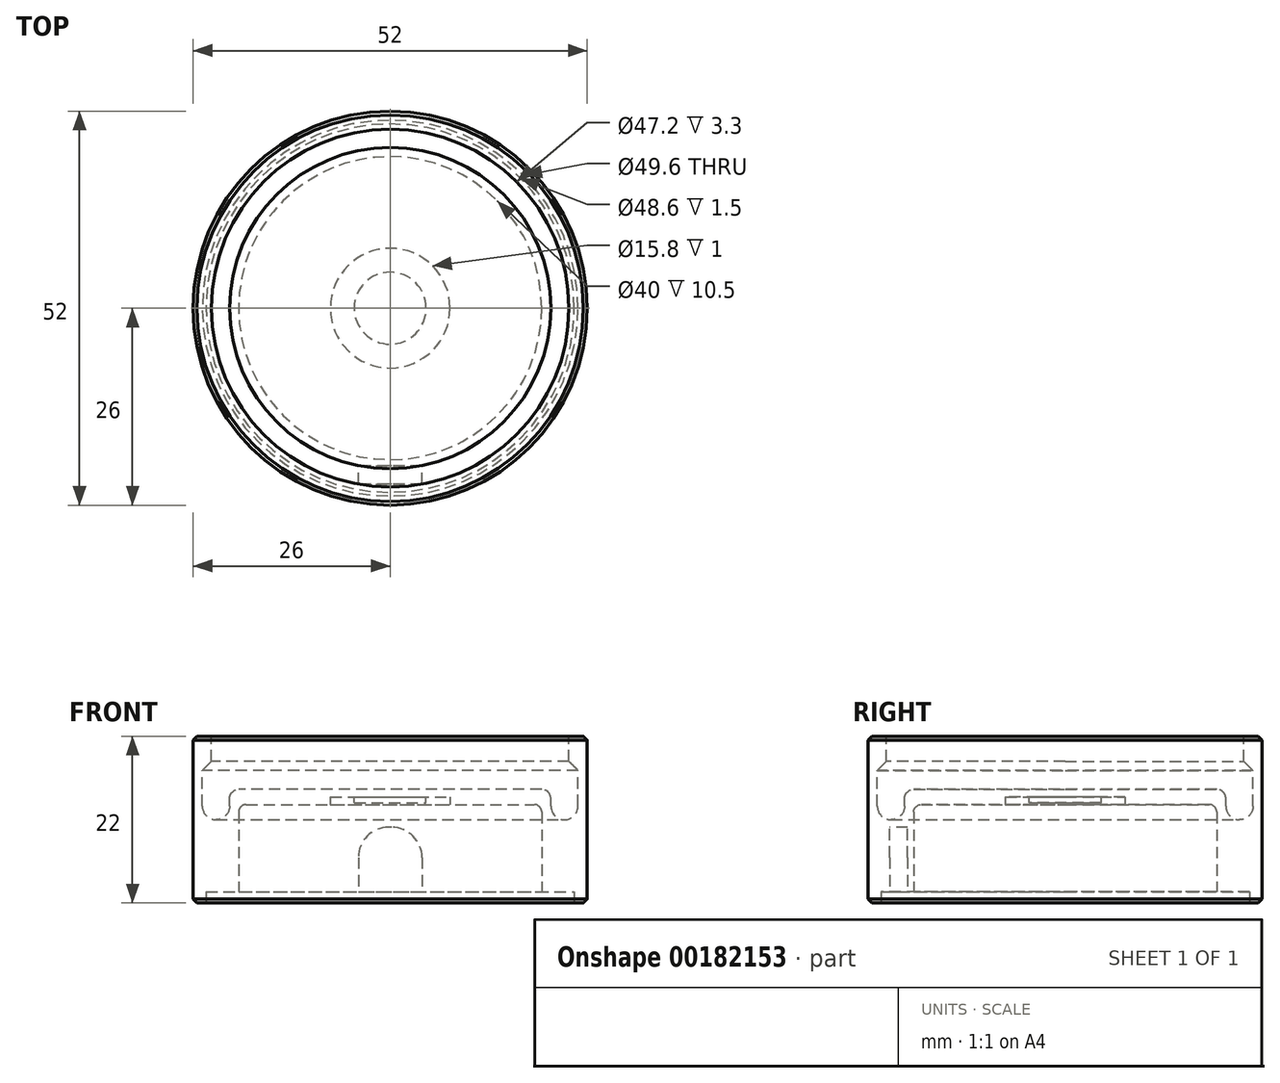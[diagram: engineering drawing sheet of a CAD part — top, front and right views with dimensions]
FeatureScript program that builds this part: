
annotation { "Feature Type Name" : "Feature", "Feature Type Description" : "" }
export const myFeature = defineFeature(function(context is Context, id is Id, definition is map)
    precondition{}
    {
        {
            var Q0;
            Q0=qCreatedBy(makeId("Top.planeOp"),FACE);
            var sketch = newSketch(context, id + "F0", { "sketchPlane" : qUnion([Q0])});
            skCircle(sketch, "E0", {"center": v(0, 0) * mm, "radius": 26 * mm});
            skSolve(sketch);
        }
        {
            var Q0;
            Q0 = qSketchRegion(id + "F0", true);
            extrude(context, id + "F1", {"entities" : qUnion([Q0]), "depth" : 22 * mm});
        }
        {
            var Q0;
            Q0=makeQuery(id+"F1.opExtrude","CAP_FACE",FACE,{"disambiguationData":[OSD([sQuery(id+"F0.wireOp",EDGE,"E0")])],"isStart":true});
            var sketch = newSketch(context, id + "F2", { "sketchPlane" : qUnion([Q0])});
            skLineSegment(sketch, "E1.bottom", {"start": v(4.2, 20.8) * mm, "end": v(-4.2, 20.8) * mm});
            skLineSegment(sketch, "E1.top", {"start": v(4.2, 23.2) * mm, "end": v(-4.2, 23.2) * mm});
            skLineSegment(sketch, "E1.left", {"start": v(4.2, 20.8) * mm, "end": v(4.2, 23.2) * mm});
            skLineSegment(sketch, "E1.right", {"start": v(-4.2, 20.8) * mm, "end": v(-4.2, 23.2) * mm});
            skPoint(sketch, "E1.middle", {"position": v(0, 22) * mm});
            skSolve(sketch);
        }
        {
            var Q0;
            Q0 = qSketchRegion(id + "F2", true);
            extrude(context, id + "F3", {"entities" : qUnion([Q0]), "operationType" : NewBodyOperationType.REMOVE, "oppositeDirection" : true, "depth" : 10 * mm});
        }
        {
            var Q0;
            Q0=makeQuery(id+"F3.boolean.opBoolean","COPY",EDGE,{"derivedFrom":makeQuery(id+"F3.opExtrude","CAP_EDGE",EDGE,{"disambiguationData":[OSD([sQuery(id+"F2.wireOp",EDGE,"E1.left")])],"isStart":false})});
            var Q1;
            Q1=makeQuery(id+"F3.boolean.opBoolean","COPY",EDGE,{"derivedFrom":makeQuery(id+"F3.opExtrude","CAP_EDGE",EDGE,{"disambiguationData":[OSD([sQuery(id+"F2.wireOp",EDGE,"E1.right")])],"isStart":false})});
            fillet(context, id + "F4", {"entities" : qUnion([Q0, Q1]), "radius" : 4 * mm, "tangentPropagation" : true, "allowEdgeOverflow" : false});
        }
        {
            var Q0;
            Q0=makeQuery(id+"F1.opExtrude","CAP_FACE",FACE,{"disambiguationData":[OSD([sQuery(id+"F0.wireOp",EDGE,"E0")])],"isStart":true});
            var sketch = newSketch(context, id + "F5", { "sketchPlane" : qUnion([Q0])});
            skCircle(sketch, "E2", {"center": v(0, 0) * mm, "radius": 20 * mm});
            skSolve(sketch);
        }
        {
            var Q0;
            Q0 = qSketchRegion(id + "F5", true);
            extrude(context, id + "F6", {"entities" : qUnion([Q0]), "operationType" : NewBodyOperationType.REMOVE, "oppositeDirection" : true, "depth" : 13 * mm});
        }
        {
            var Q0;
            Q0=makeQuery(id+"F6.boolean.opBoolean","COPY",FACE,{"derivedFrom":makeQuery(id+"F6.opExtrude","CAP_FACE",FACE,{"disambiguationData":[OSD([sQuery(id+"F5.wireOp",EDGE,"E2")])],"isStart":false})});
            var sketch = newSketch(context, id + "F7", { "sketchPlane" : qUnion([Q0])});
            skCircle(sketch, "E3", {"center": v(0, 0) * mm, "radius": 7.9 * mm});
            skSolve(sketch);
        }
        {
            var Q0;
            Q0=makeQuery(id+"F7.imprint","IMPRINT",FACE,{"disambiguationData":[TD([[makeQuery(id+"F7.imprint","IMPRINT",EDGE,{"derivedFrom":sQuery(id+"F7.wireOp",EDGE,"E3")}),1.0]])]});
            extrude(context, id + "F8", {"entities" : qUnion([Q0]), "operationType" : NewBodyOperationType.REMOVE, "oppositeDirection" : true, "depth" : 1 * mm});
        }
        {
            var Q0;
            Q0=makeQuery(id+"F8.boolean.opBoolean","COPY",FACE,{"derivedFrom":makeQuery(id+"F8.opExtrude","CAP_FACE",FACE,{"disambiguationData":[OSD([sQuery(id+"F7.wireOp",EDGE,"E3")])],"isStart":false})});
            var sketch = newSketch(context, id + "F9", { "sketchPlane" : qUnion([Q0])});
            skCircle(sketch, "E4", {"center": v(0, 0) * mm, "radius": 4.75 * mm});
            skSolve(sketch);
        }
        {
            var Q0;
            Q0 = qSketchRegion(id + "F9", true);
            extrude(context, id + "F10", {"entities" : qUnion([Q0]), "operationType" : NewBodyOperationType.ADD, "depth" : 0.8 * mm});
        }
        {
            var Q0;
            Q0=makeQuery(id+"F1.opExtrude","CAP_FACE",FACE,{"disambiguationData":[OSD([sQuery(id+"F0.wireOp",EDGE,"E0")])],"isStart":false});
            var sketch = newSketch(context, id + "F11", { "sketchPlane" : qUnion([Q0])});
            skCircle(sketch, "E5", {"center": v(0, 0) * mm, "radius": 23.6 * mm});
            skSolve(sketch);
        }
        {
            var Q0;
            Q0 = qSketchRegion(id + "F11", true);
            extrude(context, id + "F12", {"entities" : qUnion([Q0]), "operationType" : NewBodyOperationType.REMOVE, "oppositeDirection" : true, "depth" : 7 * mm});
        }
        {
            var Q0;
            Q0=makeQuery(id+"F12.boolean.opBoolean","COPY",FACE,{"derivedFrom":makeQuery(id+"F12.opExtrude","CAP_FACE",FACE,{"disambiguationData":[OSD([sQuery(id+"F11.wireOp",EDGE,"E5")])],"isStart":false})});
            var sketch = newSketch(context, id + "F13", { "sketchPlane" : qUnion([Q0])});
            skCircle(sketch, "E6.0", {"center": v(0, 0) * mm, "radius": 21.2 * mm});
            skCircle(sketch, "E7.0", {"center": v(0, 0) * mm, "radius": 24.8 * mm});
            skSolve(sketch);
        }
        {
            var Q0;
            Q0 = qSketchRegion(id + "F13", true);
            extrude(context, id + "F14", {"entities" : qUnion([Q0]), "operationType" : NewBodyOperationType.REMOVE, "oppositeDirection" : true, "depth" : 4 * mm, "hasSecondDirection" : true, "secondDirectionOppositeDirection" : false, "secondDirectionDepth" : 4 * mm});
        }
        {
            var Q0;
            Q0=makeQuery(id+"F14.boolean.opBoolean","COPY",EDGE,{"derivedFrom":makeQuery(id+"F14.opExtrude","CAP_EDGE",EDGE,{"disambiguationData":[OSD([sQuery(id+"F13.wireOp",EDGE,"E7.0")])],"isStart":false})});
            var Q1;
            Q1=makeQuery(id+"F14.boolean.opBoolean","COPY",EDGE,{"derivedFrom":makeQuery(id+"F14.opExtrude","CAP_EDGE",EDGE,{"disambiguationData":[OSD([sQuery(id+"F13.wireOp",EDGE,"E6.0")])],"isStart":false})});
            fillet(context, id + "F15", {"entities" : qUnion([Q0, Q1]), "radius" : 1.8 * mm, "tangentPropagation" : true, "allowEdgeOverflow" : false});
        }
        {
            var Q0;
            Q0=makeQuery(id+"F14.boolean.opBoolean","COPY",EDGE,{"derivedFrom":makeQuery(id+"F14.opExtrude","CAP_EDGE",EDGE,{"disambiguationData":[OSD([sQuery(id+"F13.wireOp",EDGE,"E6.0")])],"isStart":true})});
            var Q1;
            Q1=makeQuery(id+"F14.boolean.opBoolean","INTERSECT",EDGE,{"derivedFrom":[makeQuery(id+"F12.boolean.opBoolean","COPY",FACE,{"derivedFrom":makeQuery(id+"F12.opExtrude","CAP_FACE",FACE,{"disambiguationData":[OSD([sQuery(id+"F11.wireOp",EDGE,"E5")])],"isStart":false})}),makeQuery(id+"F14.opExtrude","SWEPT_FACE",FACE,{"disambiguationData":[OSD([sQuery(id+"F13.wireOp",EDGE,"E6.0")])]})]});
            fillet(context, id + "F16", {"entities" : qUnion([Q0, Q1]), "radius" : 1.2 * mm, "tangentPropagation" : true, "allowEdgeOverflow" : false});
        }
        {
            var Q0;
            Q0=makeQuery(id+"F14.boolean.opBoolean","COPY",EDGE,{"derivedFrom":makeQuery(id+"F14.opExtrude","CAP_EDGE",EDGE,{"disambiguationData":[OSD([sQuery(id+"F13.wireOp",EDGE,"E7.0")])],"isStart":true})});
            chamfer(context, id + "F17", {"entities" : qUnion([Q0]), "width" : 1.5 * mm, "tangentPropagation" : true});
        }
        {
            var Q0;
            Q0=makeQuery(id+"F6.boolean.opBoolean","COPY",EDGE,{"derivedFrom":makeQuery(id+"F6.opExtrude","CAP_EDGE",EDGE,{"disambiguationData":[OSD([sQuery(id+"F5.wireOp",EDGE,"E2")])],"isStart":false})});
            fillet(context, id + "F18", {"entities" : qUnion([Q0]), "radius" : 1 * mm, "tangentPropagation" : true, "allowEdgeOverflow" : false});
        }
        {
            var Q0;
            Q0=makeQuery(id+"F1.opExtrude","CAP_EDGE",EDGE,{"disambiguationData":[OSD([sQuery(id+"F0.wireOp",EDGE,"E0")])],"isStart":true});
            var Q1;
            Q1=makeQuery(id+"F1.opExtrude","CAP_EDGE",EDGE,{"disambiguationData":[OSD([sQuery(id+"F0.wireOp",EDGE,"E0")])],"isStart":false});
            chamfer(context, id + "F19", {"entities" : qUnion([Q0, Q1]), "width" : 0.5 * mm, "tangentPropagation" : true});
        }
        {
            var Q0;
            Q0=makeQuery(id+"F1.opExtrude","CAP_FACE",FACE,{"disambiguationData":[OSD([sQuery(id+"F0.wireOp",EDGE,"E0")])],"isStart":true});
            var sketch = newSketch(context, id + "F20", { "sketchPlane" : qUnion([Q0])});
            skCircle(sketch, "E8", {"center": v(0, 0) * mm, "radius": 24.3 * mm});
            skSolve(sketch);
        }
        {
            var Q0;
            Q0 = qSketchRegion(id + "F20", true);
            extrude(context, id + "F21", {"entities" : qUnion([Q0]), "operationType" : NewBodyOperationType.REMOVE, "oppositeDirection" : true, "depth" : 1.5 * mm});
        }
    });
